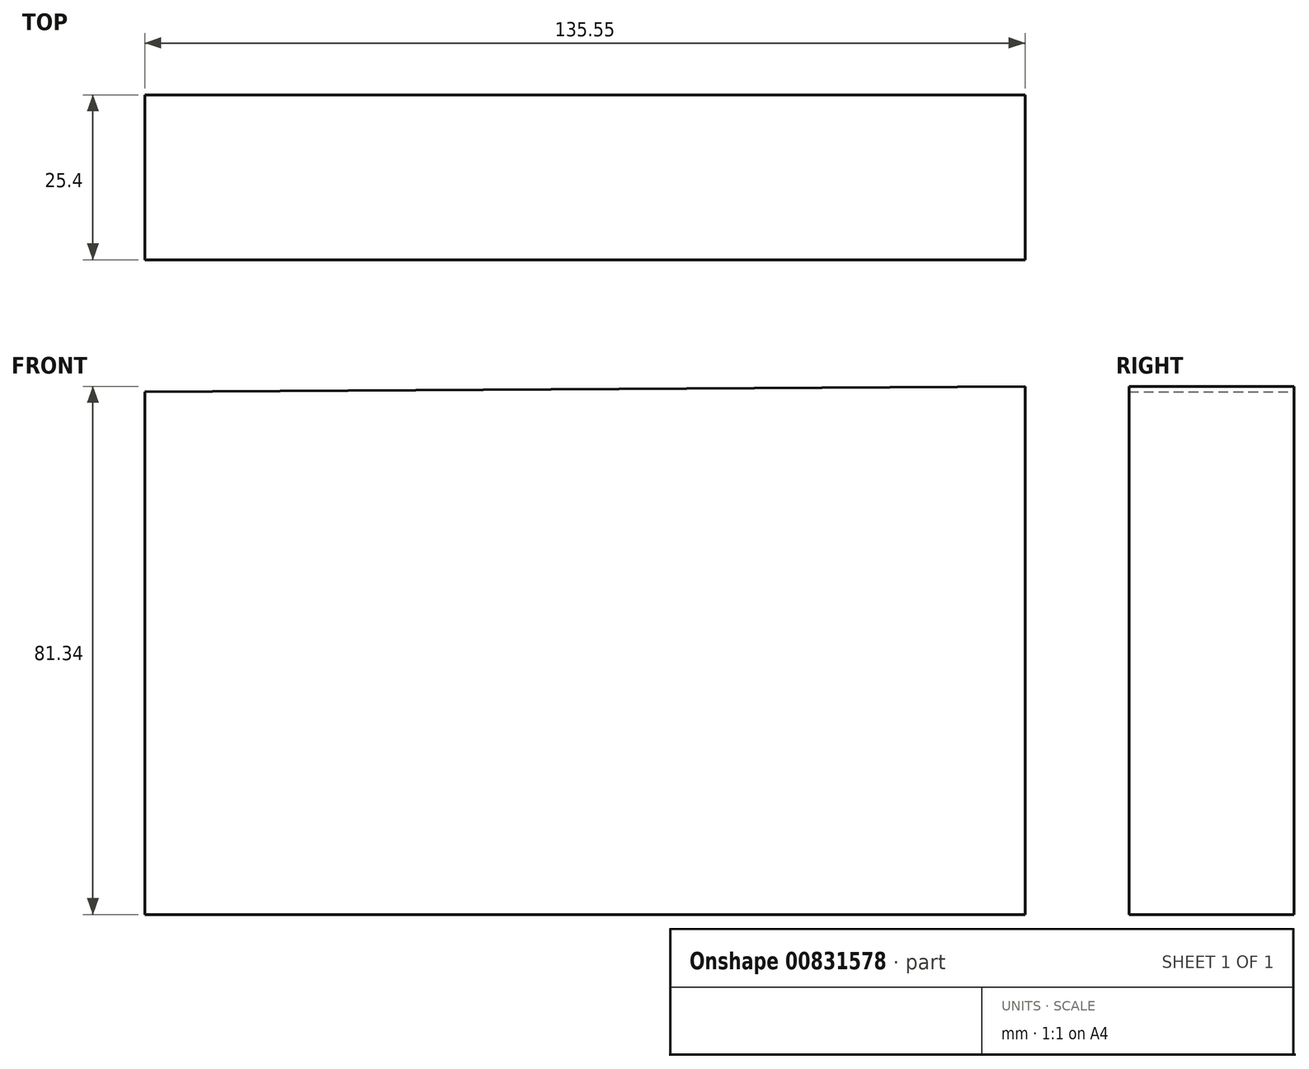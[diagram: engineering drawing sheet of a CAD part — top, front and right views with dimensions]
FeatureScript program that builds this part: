
annotation { "Feature Type Name" : "Feature", "Feature Type Description" : "" }
export const myFeature = defineFeature(function(context is Context, id is Id, definition is map)
    precondition{}
    {
        {
            var Q0;
            Q0=qCreatedBy(makeId("Front.planeOp"),FACE);
            var sketch = newSketch(context, id + "F0", { "sketchPlane" : qUnion([Q0])});
            skLineSegment(sketch, "E0", {"start": v(-92.78, 41.84) * mm, "end": v(-92.78, -38.67) * mm});
            skLineSegment(sketch, "E1", {"start": v(-92.78, -38.67) * mm, "end": v(42.77, -38.67) * mm});
            skLineSegment(sketch, "E2", {"start": v(42.77, -38.67) * mm, "end": v(42.77, 42.67) * mm});
            skLineSegment(sketch, "E3", {"start": v(42.77, 42.67) * mm, "end": v(-92.78, 41.84) * mm});
            skSolve(sketch);
        }
        {
            var Q0;
            Q0 = qSketchRegion(id + "F0", true);
            extrude(context, id + "F1", {"entities" : qUnion([Q0]), "depth" : 25.4 * mm, "offsetDistance" : 25.4 * mm});
        }
    });
